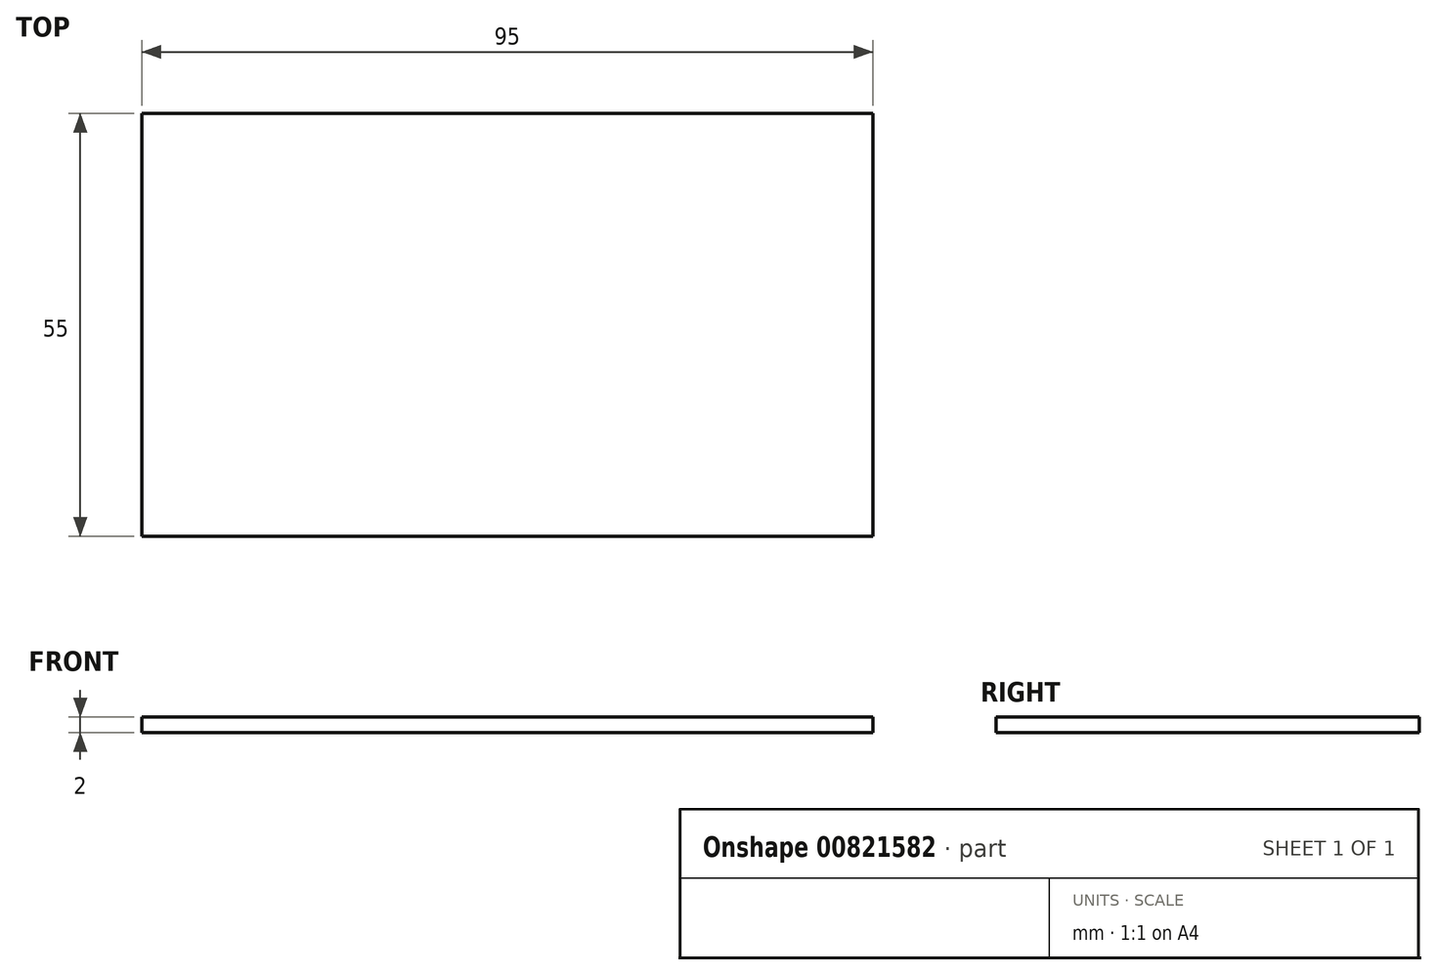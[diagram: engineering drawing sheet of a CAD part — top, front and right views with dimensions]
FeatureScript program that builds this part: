
annotation { "Feature Type Name" : "Feature", "Feature Type Description" : "" }
export const myFeature = defineFeature(function(context is Context, id is Id, definition is map)
    precondition{}
    {
        {
            var Q0;
            Q0=qCreatedBy(makeId("Top.planeOp"),FACE);
            var sketch = newSketch(context, id + "F0", { "sketchPlane" : qUnion([Q0])});
            skLineSegment(sketch, "E0.bottom", {"start": v(-29.85, 22.42) * mm, "end": v(65.15, 22.42) * mm});
            skLineSegment(sketch, "E0.top", {"start": v(-29.85, -32.58) * mm, "end": v(65.15, -32.58) * mm});
            skLineSegment(sketch, "E0.left", {"start": v(-29.85, 22.42) * mm, "end": v(-29.85, -32.58) * mm});
            skLineSegment(sketch, "E0.right", {"start": v(65.15, 22.42) * mm, "end": v(65.15, -32.58) * mm});
            skSolve(sketch);
        }
        {
            var Q0;
            Q0 = qSketchRegion(id + "F0", true);
            var Q1;
            Q1 = qSketchRegion(id + "FyqUGhpdcE1HlKW_0", true);
            extrude(context, id + "F1", {"entities" : qUnion([Q0, Q1]), "depth" : 2 * mm, "offsetDistance" : 25 * mm});
        }
    });
